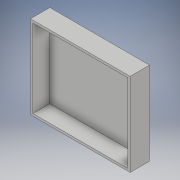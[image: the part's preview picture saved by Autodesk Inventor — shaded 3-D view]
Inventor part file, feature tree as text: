
AUTODESK INVENTOR PART (.ipt)
format: ipt  version: 2018 (Build 220112000, 112)  size: 104,960 bytes
history: native  units: in
note: dims shown in document units (in); Inventor stores cm internally (conversion verified against a paired STEP export)
features: extrude x2, sketch x2
ambient origin geometry x8: Origin, YZ Plane, XZ Plane, XY Plane, X Axis, Y Axis, Z Axis, Center Point
bodies: Solid1 (feature_tree)
feature tree (4):
  extrude  "Extrusion1"  Depth=25.81in
  extrude  "Extrusion2"  Depth=0.75in
  sketch  "Sketch1"  dims[d0=30.87in d1=25.81in]
  sketch  "Sketch2"  dims[d2=0.75in d3=0.0in d4=0.75in d5=5.25in d6=0.0in]
